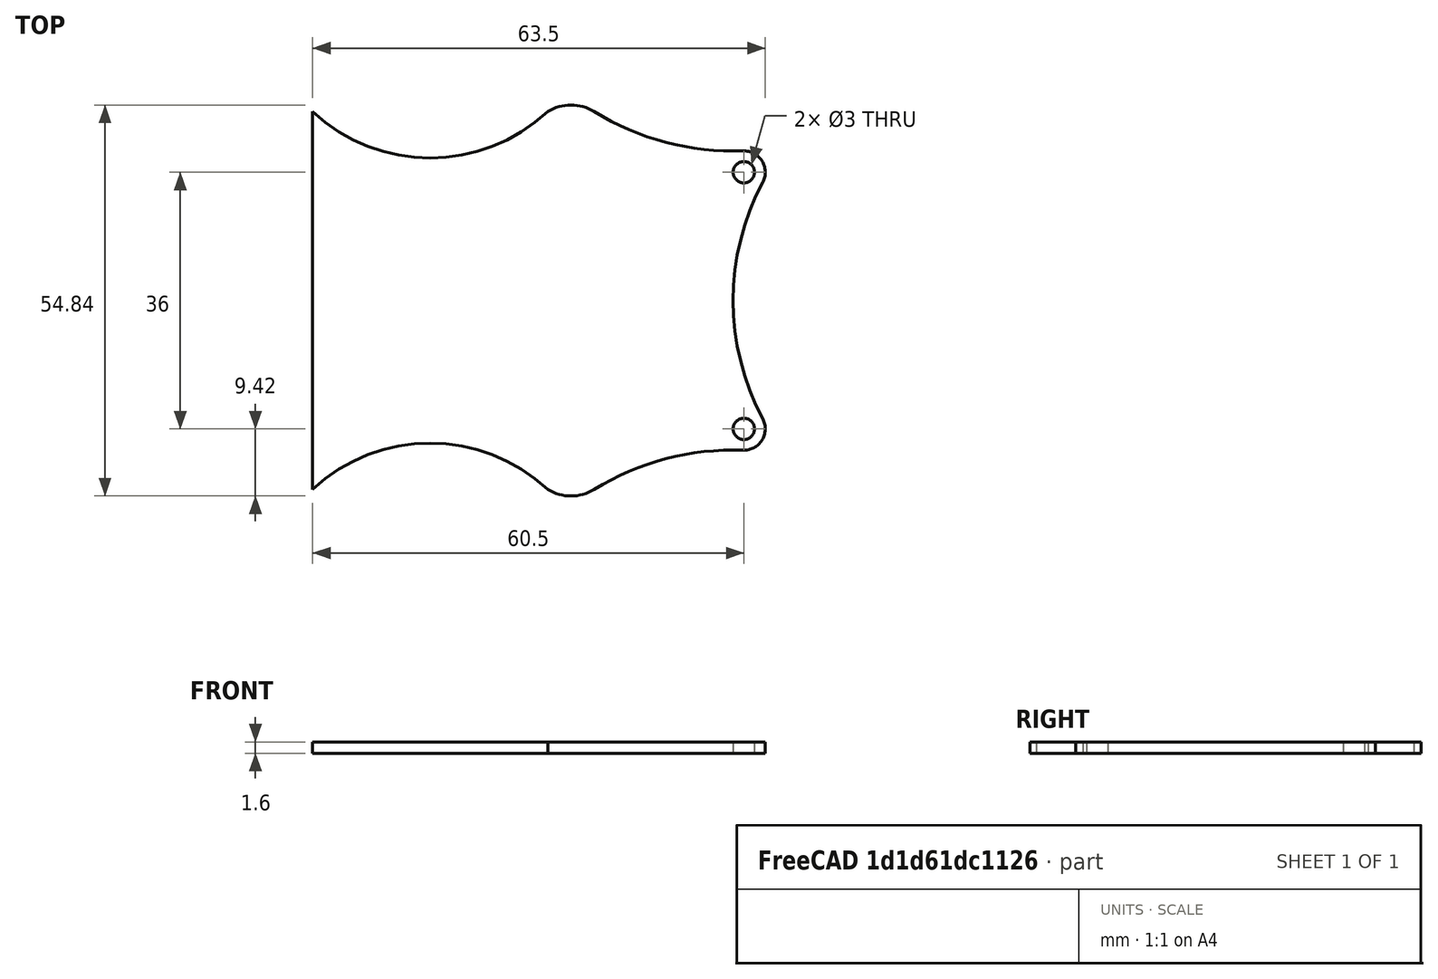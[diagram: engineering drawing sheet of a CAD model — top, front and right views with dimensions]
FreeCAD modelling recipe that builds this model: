
FCSTD DOCUMENT  (FreeCAD 0.19R24366 (Git))
Label: nixiePanelShape
License: All rights reserved
LicenseURL: http://en.wikipedia.org/wiki/All_rights_reserved
objects: Sketcher::SketchObject×1, PartDesign::Pad×1, PartDesign::Body×1
note: 4 computed .brp shape members not serialized (recipe doc carries the construction recipe); baked Part::Feature solids carry a one-line shape summary decoded from their .brp

FEATURE [Sketcher::SketchObject] Sketch
  FullyConstrained = true
  MapMode = 5
  Support = -> [XY_Plane]
  sketch-geometry (63):
    g0: LineSegment StartX=0 StartY=0 StartZ=0 EndX=85 EndY=0 EndZ=0
    g1: LineSegment StartX=85 StartY=0 StartZ=0 EndX=85 EndY=53 EndZ=0
    g2: LineSegment StartX=85 StartY=53 StartZ=0 EndX=0 EndY=53 EndZ=0
    g3: LineSegment StartX=0 StartY=53 StartZ=0 EndX=0 EndY=0 EndZ=0
    g4: LineSegment StartX=2.5 StartY=44.5 StartZ=0 EndX=82.5 EndY=44.5 EndZ=0
    g5: LineSegment StartX=82.5 StartY=44.5 StartZ=0 EndX=82.5 EndY=8.5 EndZ=0
    g6: LineSegment StartX=82.5 StartY=8.5 StartZ=0 EndX=2.5 EndY=8.5 EndZ=0
    g7: LineSegment StartX=2.5 StartY=8.5 StartZ=0 EndX=2.5 EndY=44.5 EndZ=0
    g8: LineSegment StartX=2.5 StartY=8.5 StartZ=0 EndX=0 EndY=0 EndZ=0
    g9: LineSegment StartX=82.5 StartY=8.5 StartZ=0 EndX=85 EndY=0 EndZ=0
    g10: LineSegment StartX=82.5 StartY=44.5 StartZ=0 EndX=85 EndY=53 EndZ=0
    g11: LineSegment StartX=0 StartY=53 StartZ=0 EndX=2.5 EndY=44.5 EndZ=0
    g12: LineSegment StartX=-7.5 StartY=-23.5 StartZ=0 EndX=92.5 EndY=-23.5 EndZ=0
    g13: LineSegment StartX=92.5 StartY=-23.5 StartZ=0 EndX=92.5 EndY=76.5 EndZ=0
    g14: LineSegment StartX=92.5 StartY=76.5 StartZ=0 EndX=-7.5 EndY=76.5 EndZ=0
    g15: LineSegment StartX=-7.5 StartY=76.5 StartZ=0 EndX=-7.5 EndY=-23.5 EndZ=0
    g16: LineSegment StartX=0 StartY=0 StartZ=0 EndX=-7.5 EndY=-23.5 EndZ=0
    g17: LineSegment StartX=85 StartY=0 StartZ=0 EndX=92.5 EndY=-23.5 EndZ=0
    g18: LineSegment StartX=-7.5 StartY=76.5 StartZ=0 EndX=0 EndY=53 EndZ=0
    g19: LineSegment StartX=92.5 StartY=76.5 StartZ=0 EndX=85 EndY=53 EndZ=0
    g20: Circle CenterX=86.5 CenterY=44.5 CenterZ=0 NormalX=0 NormalY=0 NormalZ=1 AngleXU=0 Radius=1.5
    g21: Circle CenterX=86.5 CenterY=8.5 CenterZ=0 NormalX=0 NormalY=0 NormalZ=1 AngleXU=0 Radius=1.5
    g22: Circle CenterX=-1.5 CenterY=8.5 CenterZ=0 NormalX=0 NormalY=0 NormalZ=1 AngleXU=0 Radius=1.5
    g23: Circle CenterX=-1.5 CenterY=44.5 CenterZ=0 NormalX=0 NormalY=0 NormalZ=1 AngleXU=0 Radius=1.5
    g24: Circle CenterX=-1.5 CenterY=44.5 CenterZ=0 NormalX=0 NormalY=0 NormalZ=1 AngleXU=0 Radius=3
    g25: Circle CenterX=-1.5 CenterY=8.5 CenterZ=0 NormalX=0 NormalY=0 NormalZ=1 AngleXU=0 Radius=3
    g26: Circle CenterX=86.5 CenterY=8.5 CenterZ=0 NormalX=0 NormalY=0 NormalZ=1 AngleXU=0 Radius=3
    g27: Circle CenterX=86.5 CenterY=44.5 CenterZ=0 NormalX=0 NormalY=0 NormalZ=1 AngleXU=0 Radius=3
    g28: Circle CenterX=120.25 CenterY=26.5 CenterZ=0 NormalX=0 NormalY=0 NormalZ=1 AngleXU=0 Radius=35.25
    g29: Circle CenterX=-35.25 CenterY=26.5 CenterZ=0 NormalX=0 NormalY=0 NormalZ=1 AngleXU=0 Radius=35.25
    g30: LineSegment StartX=0 StartY=63 StartZ=0 EndX=19.5 EndY=63 EndZ=0
    g31: LineSegment StartX=19.5 StartY=63 StartZ=0 EndX=26 EndY=63 EndZ=0
    g32: LineSegment StartX=26 StartY=63 StartZ=0 EndX=59 EndY=63 EndZ=0
    g33: LineSegment StartX=59 StartY=63 StartZ=0 EndX=65.5 EndY=63 EndZ=0
    g34: LineSegment StartX=65.5 StartY=63 StartZ=0 EndX=85 EndY=63 EndZ=0
    g35: LineSegment StartX=19.5 StartY=76.5 StartZ=0 EndX=19.5 EndY=-23.5 EndZ=0
    g36: LineSegment StartX=26 StartY=76.5 StartZ=0 EndX=26 EndY=-23.5 EndZ=0
    g37: LineSegment StartX=59 StartY=76.5 StartZ=0 EndX=59 EndY=-23.5 EndZ=0
    g38: LineSegment StartX=65.5 StartY=76.5 StartZ=0 EndX=65.5 EndY=-23.5 EndZ=0
    g39: Circle CenterX=0 CenterY=-31.6289 CenterZ=0 NormalX=0 NormalY=0 NormalZ=1 AngleXU=0 Radius=37.1569
    g40: LineSegment StartX=2.5 StartY=8.5 StartZ=0 EndX=19.5 EndY=-3.6e-15 EndZ=0
    g41: Circle CenterX=85 CenterY=-31.6289 CenterZ=0 NormalX=0 NormalY=0 NormalZ=1 AngleXU=0 Radius=37.1569
    g42: Circle CenterX=0 CenterY=84.6289 CenterZ=0 NormalX=0 NormalY=0 NormalZ=1 AngleXU=0 Radius=37.1569
    g43: Circle CenterX=85 CenterY=84.6289 CenterZ=0 NormalX=0 NormalY=0 NormalZ=1 AngleXU=0 Radius=37.1569
    g44: LineSegment StartX=26 StartY=6.5 StartZ=0 EndX=59 EndY=6.5 EndZ=0
    g45: LineSegment StartX=26 StartY=46.5 StartZ=0 EndX=59 EndY=46.5 EndZ=0
    g46: LineSegment StartX=26 StartY=53 StartZ=0 EndX=42.5 EndY=46.5 EndZ=0
    g47: LineSegment StartX=42.5 StartY=46.5 StartZ=0 EndX=59 EndY=53 EndZ=0
    g48: LineSegment StartX=26 StartY=-4.4e-15 StartZ=0 EndX=42.5 EndY=6.5 EndZ=0
    g49: LineSegment StartX=42.5 StartY=6.5 StartZ=0 EndX=59 EndY=0 EndZ=0
    g50: Circle CenterX=42.5 CenterY=-17.6923 CenterZ=0 NormalX=0 NormalY=0 NormalZ=1 AngleXU=0 Radius=24.1923
    g51: Circle CenterX=42.5 CenterY=70.6923 CenterZ=0 NormalX=0 NormalY=0 NormalZ=1 AngleXU=0 Radius=24.1923
    g52: ArcOfCircle CenterX=22.75 CenterY=5.27149 CenterZ=0 NormalX=0 NormalY=0 NormalZ=1 AngleXU=0 Radius=6.19282 StartAngle=4.15991 EndAngle=5.26487
    g53: ArcOfCircle CenterX=42.5 CenterY=-17.6923 CenterZ=0 NormalX=0 NormalY=0 NormalZ=1 AngleXU=0 Radius=24.1923 StartAngle=0.820255 EndAngle=2.32134
    g54: ArcOfCircle CenterX=62.25 CenterY=5.27149 CenterZ=0 NormalX=0 NormalY=0 NormalZ=1 AngleXU=0 Radius=6.19282 StartAngle=4.15991 EndAngle=5.26487
    g55: ArcOfCircle CenterX=85 CenterY=-31.6289 CenterZ=0 NormalX=0 NormalY=0 NormalZ=1 AngleXU=0 Radius=37.1569 StartAngle=1.53343 EndAngle=2.12328
    g56: ArcOfCircle CenterX=120.25 CenterY=26.5 CenterZ=0 NormalX=0 NormalY=0 NormalZ=1 AngleXU=0 Radius=35.25 StartAngle=2.65164 EndAngle=3.63155
    g57: ArcOfCircle CenterX=86.5 CenterY=8.5 CenterZ=0 NormalX=0 NormalY=0 NormalZ=1 AngleXU=0 Radius=3 StartAngle=4.67503 EndAngle=6.77314
    g58: ArcOfCircle CenterX=85 CenterY=84.6289 CenterZ=0 NormalX=0 NormalY=0 NormalZ=1 AngleXU=0 Radius=37.1569 StartAngle=4.15991 EndAngle=4.74975
    g59: ArcOfCircle CenterX=86.5 CenterY=44.5 CenterZ=0 NormalX=0 NormalY=0 NormalZ=1 AngleXU=0 Radius=3 StartAngle=5.79323 EndAngle=7.89134
    g60: ArcOfCircle CenterX=42.5 CenterY=70.6923 CenterZ=0 NormalX=0 NormalY=0 NormalZ=1 AngleXU=0 Radius=24.1923 StartAngle=3.96185 EndAngle=5.46293
    g61: ArcOfCircle CenterX=62.25 CenterY=47.7285 CenterZ=0 NormalX=0 NormalY=0 NormalZ=1 AngleXU=0 Radius=6.19283 StartAngle=1.01832 EndAngle=2.12328
    g62: LineSegment StartX=26 StartY=-4.4e-15 StartZ=0 EndX=26 EndY=53 EndZ=0
  constraints (190):
    c: Coincident(g0,g1)
    c: Coincident(g1,g2)
    c: Coincident(g2,g3)
    c: Coincident(g3,g0)
    c: Horizontal(g0)
    c: Horizontal(g2)
    c: Vertical(g1)
    c: Vertical(g3)
    c: Coincident(g0,g-1)
    c: Coincident(g4,g5)
    c: Coincident(g5,g6)
    c: Coincident(g6,g7)
    c: Coincident(g7,g4)
    c: Horizontal(g4)
    c: Horizontal(g6)
    c: Vertical(g5)
    c: Vertical(g7)
    c: Distance(g4) = 80
    c: Distance(g7) = 36
    c: Distance(g3) = 53
    c: Distance(g2) = 85
    c: Coincident(g8,g6)
    c: Coincident(g8,g-1)
    c: Coincident(g9,g5)
    c: Coincident(g10,g4)
    c: Coincident(g10,g1)
    c: Coincident(g11,g2)
    c: Coincident(g11,g4)
    c: Coincident(g9,g0)
    c: Equal(g11,g8)
    c: Equal(g8,g9)
    c: Coincident(g12,g13)
    c: Coincident(g13,g14)
    c: Coincident(g14,g15)
    c: Coincident(g15,g12)
    c: Horizontal(g12)
    c: Horizontal(g14)
    c: Vertical(g13)
    c: Vertical(g15)
    c: Equal(g14,g15)
    c: Distance(g15) = 100
    c: Coincident(g16,g-1)
    c: Coincident(g16,g12)
    c: Coincident(g17,g0)
    c: Coincident(g17,g12)
    c: Coincident(g18,g14)
    c: Coincident(g18,g2)
    c: Coincident(g19,g13)
    c: Coincident(g19,g1)
    c: Equal(g17,g16)
    c: Equal(g16,g18)
    c: Equal(g22,g23)
    c: Equal(g23,g20)
    c: Equal(g20,g21)
    c: PointOnObject(g22,g6)
    c: PointOnObject(g21,g6)
    c: PointOnObject(g20,g4)
    c: PointOnObject(g23,g4)
    c: Radius(g20) = 1.5
    c: Tangent(g22,g3)
    c: Tangent(g23,g3)
    c: Tangent(g20,g1)
    c: Tangent(g21,g1)
    c: Coincident(g24,g23)
    c: Coincident(g25,g22)
    c: Coincident(g26,g21)
    c: Coincident(g27,g20)
    c: Equal(g24,g25)
    c: Equal(g25,g26)
    c: Equal(g26,g27)
    c: Radius(g24) = 3
    c: Tangent(g28,g27)
    c: Tangent(g28,g26)
    c: Tangent(g28,g1)
    c: Tangent(g29,g24)
    c: Tangent(g29,g25)
    c: Tangent(g29,g3)
    c: PointOnObject(g30,g-2)
    c: Horizontal(g30)
    c: Coincident(g30,g31)
    c: Horizontal(g31)
    c: Coincident(g31,g32)
    c: Horizontal(g32)
    c: Coincident(g32,g33)
    c: Horizontal(g33)
    c: Coincident(g33,g34)
    c: Horizontal(g34)
    c: Equal(g30,g34)
    c: Equal(g31,g33)
    c: Distance(g32) = 33
    c: Distance(g30) = 19.5
    c: Distance(g30,g2) = 10
    c: PointOnObject(g35,g14)
    c: PointOnObject(g35,g12)
    c: Vertical(g35)
    c: PointOnObject(g36,g14)
    c: PointOnObject(g36,g12)
    c: Vertical(g36)
    c: PointOnObject(g37,g14)
    c: PointOnObject(g37,g12)
    c: Vertical(g37)
    c: PointOnObject(g38,g14)
    c: PointOnObject(g38,g12)
    c: Vertical(g38)
    c: PointOnObject(g30,g35)
    c: PointOnObject(g31,g36)
    c: PointOnObject(g32,g37)
    c: PointOnObject(g33,g38)
    c: PointOnObject(g39,g-2)
    c: Tangent(g39,g25)
    c: Coincident(g40,g6)
    c: PointOnObject(g40,g0)
    c: PointOnObject(g40,g35)
    c: PointOnObject(g40,g39)
    c: Tangent(g26,g41)
    c: PointOnObject(g41,g1)
    c: Equal(g39,g41)
    c: PointOnObject(g34,g1)
    c: PointOnObject(g42,g-2)
    c: PointOnObject(g43,g1)
    c: Tangent(g43,g27)
    c: Tangent(g42,g24)
    c: Equal(g42,g43)
    c: Equal(g43,g39)
    c: PointOnObject(g44,g36)
    c: PointOnObject(g44,g37)
    c: Horizontal(g44)
    c: PointOnObject(g45,g36)
    c: PointOnObject(g45,g37)
    c: Horizontal(g45)
    c: Distance(g45,g4) = 2
    c: Distance(g44,g6) = 2
    c: PointOnObject(g46,g2)
    c: PointOnObject(g46,g45)
    c: PointOnObject(g47,g2)
    c: PointOnObject(g46,g36)
    c: PointOnObject(g47,g37)
    c: Equal(g47,g46)
    c: Coincident(g46,g47)
    c: PointOnObject(g48,g0)
    c: PointOnObject(g48,g44)
    c: Coincident(g48,g49)
    c: PointOnObject(g49,g0)
    c: PointOnObject(g48,g36)
    c: PointOnObject(g49,g37)
    c: Equal(g49,g48)
    c: PointOnObject(g48,g50)
    c: PointOnObject(g48,g50)
    c: PointOnObject(g49,g50)
    c: PointOnObject(g46,g51)
    c: PointOnObject(g47,g51)
    c: PointOnObject(g46,g51)
    c: Coincident(g52,g40)
    c: Coincident(g52,g48)
    c: Tangent(g52,g39)
    c: Coincident(g53,g52)
    c: Coincident(g53,g49)
    c: PointOnObject(g48,g53)
    c: Coincident(g54,g53)
    c: PointOnObject(g54,g41)
    c: PointOnObject(g54,g38)
    c: Tangent(g54,g41)
    c: Coincident(g55,g54)
    c: PointOnObject(g55,g26)
    c: Tangent(g55,g26)
    c: PointOnObject(g55,g41)
    c: PointOnObject(g56,g26)
    c: Tangent(g56,g26)
    c: PointOnObject(g56,g27)
    c: PointOnObject(g56,g28)
    c: PointOnObject(g56,g28)
    c: Coincident(g57,g55)
    c: Coincident(g56,g57)
    c: Tangent(g57,g28)
    c: PointOnObject(g58,g38)
    c: PointOnObject(g58,g2)
    c: PointOnObject(g58,g27)
    c: PointOnObject(g58,g43)
    c: Tangent(g58,g27)
    c: Coincident(g56,g59)
    c: Coincident(g59,g58)
    c: Tangent(g59,g43)
    c: Coincident(g61,g58)
    c: Coincident(g61,g47)
    c: Tangent(g61,g43)
    c: Coincident(g60,g61)
    c: Coincident(g60,g46)
    c: Tangent(g60,g51)
    c: Coincident(g62,g53)
    c: Coincident(g62,g60)
FEATURE [PartDesign::Pad] Pad
  Direction = (1,1,1)
  Length = 1.6
  Length2 = 100
  Profile = -> Sketch
  Refine = true
  Type = 0
FEATURE [PartDesign::Body] Body
  Group = -> [Sketch,Pad]
  Origin = -> Origin
  Tip = -> Pad
